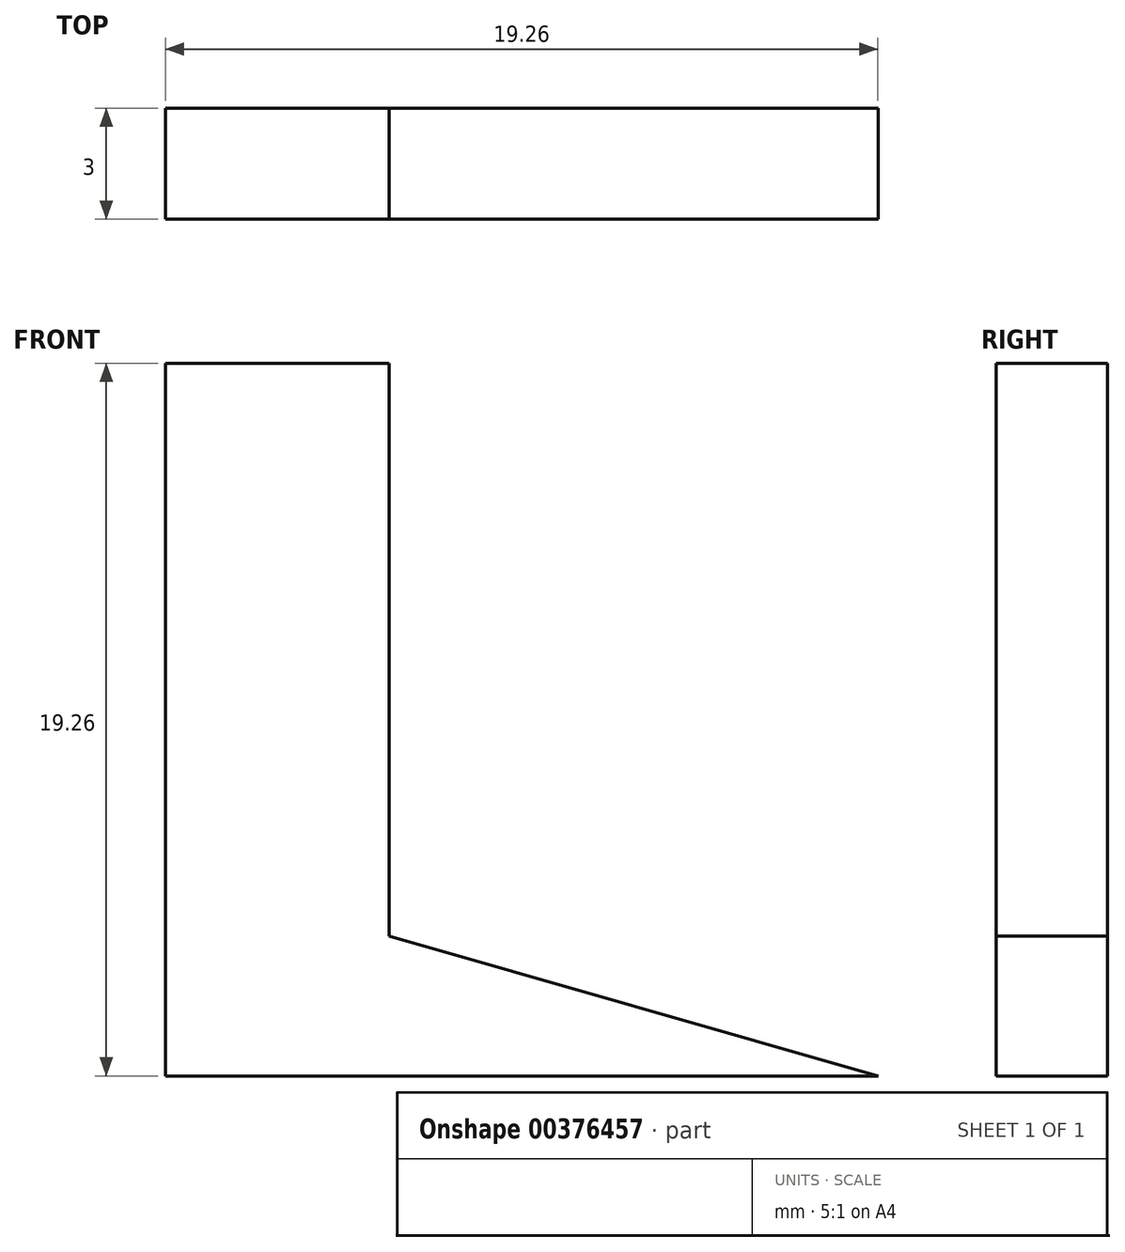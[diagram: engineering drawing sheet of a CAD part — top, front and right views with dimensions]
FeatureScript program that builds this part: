
annotation { "Feature Type Name" : "Feature", "Feature Type Description" : "" }
export const myFeature = defineFeature(function(context is Context, id is Id, definition is map)
    precondition{}
    {
        {
            var Q0;
            Q0=qCreatedBy(makeId("Front.planeOp"),FACE);
            var sketch = newSketch(context, id + "F0", { "sketchPlane" : qUnion([Q0])});
            skLineSegment(sketch, "E0", {"start": v(0, 0) * mm, "end": v(0, 19.26) * mm});
            skLineSegment(sketch, "E1", {"start": v(0, 0) * mm, "end": v(19.26, 0) * mm});
            skLineSegment(sketch, "E2", {"start": v(19.26, 0) * mm, "end": v(6.04, 3.78) * mm});
            skLineSegment(sketch, "E3", {"start": v(6.04, 3.78) * mm, "end": v(6.04, 19.26) * mm});
            skLineSegment(sketch, "E4", {"start": v(0, 19.26) * mm, "end": v(6.04, 19.26) * mm});
            skSolve(sketch);
        }
        {
            var Q0;
            Q0 = qSketchRegion(id + "F0", true);
            extrude(context, id + "F1", {"entities" : qUnion([Q0]), "depth" : 3 * mm});
        }
    });
